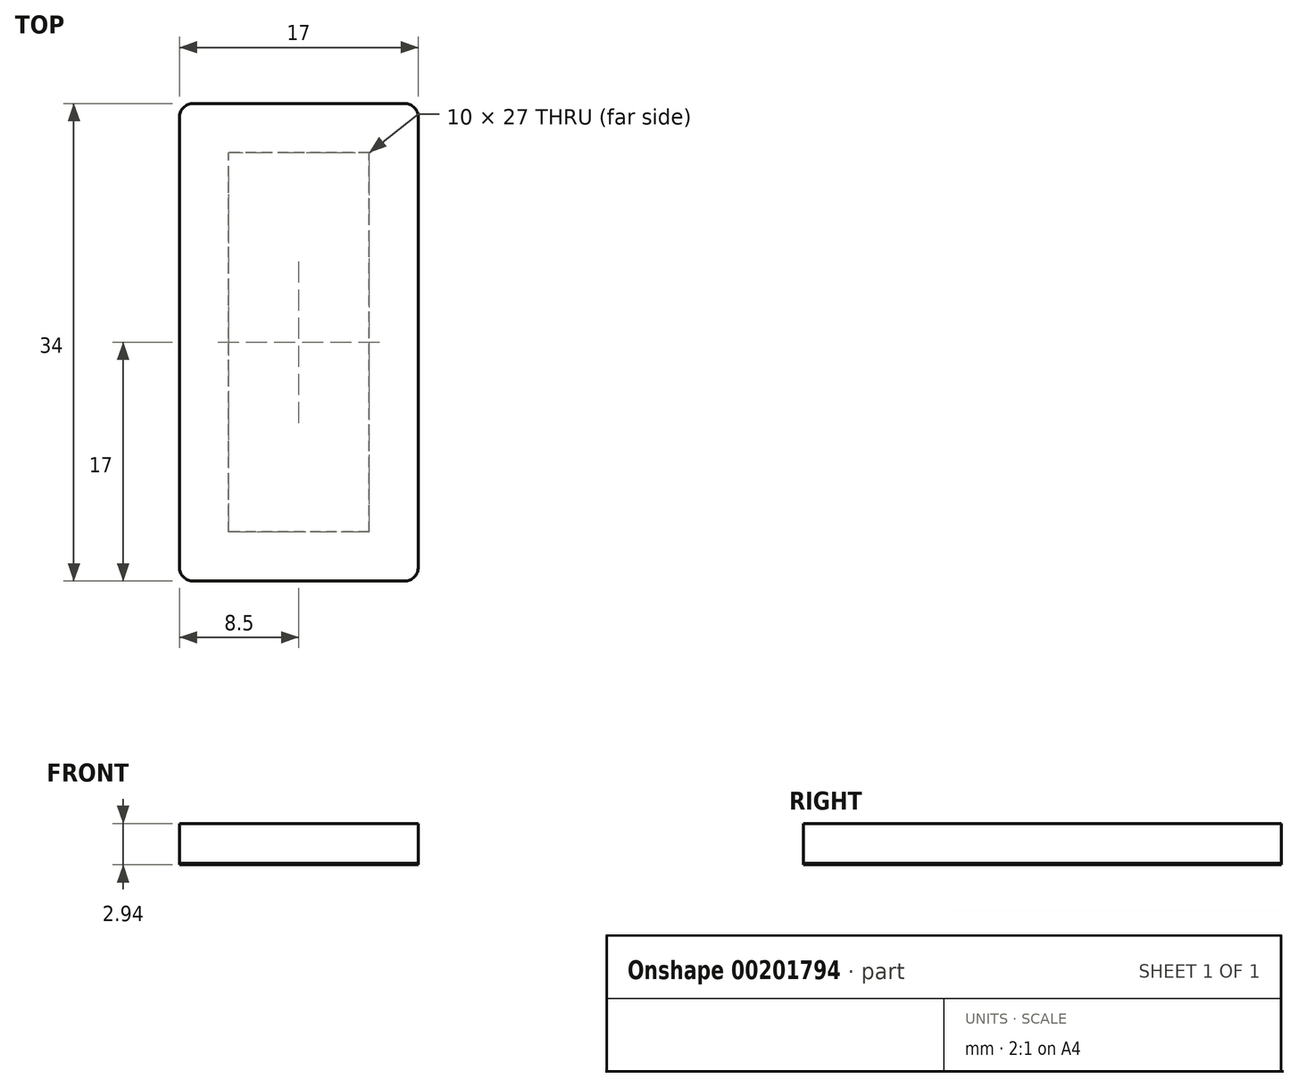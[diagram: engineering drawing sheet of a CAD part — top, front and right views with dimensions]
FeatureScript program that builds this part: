
annotation { "Feature Type Name" : "Feature", "Feature Type Description" : "" }
export const myFeature = defineFeature(function(context is Context, id is Id, definition is map)
    precondition{}
    {
        {
            var Q0;
            Q0=qCreatedBy(makeId("Top.planeOp"),FACE);
            var sketch = newSketch(context, id + "F0", { "sketchPlane" : qUnion([Q0])});
            skLineSegment(sketch, "E0", {"start": v(0, 53.35) * mm, "end": v(0, -57.86) * mm, "construction": true});
            skLineSegment(sketch, "E1", {"start": v(-67.38, 0) * mm, "end": v(68.88, 0) * mm, "construction": true});
            skLineSegment(sketch, "E2.bottom", {"start": v(-8.5, 17) * mm, "end": v(8.5, 17) * mm});
            skLineSegment(sketch, "E2.top", {"start": v(-8.5, -17) * mm, "end": v(8.5, -17) * mm});
            skLineSegment(sketch, "E2.left", {"start": v(-8.5, 17) * mm, "end": v(-8.5, -17) * mm});
            skLineSegment(sketch, "E2.right", {"start": v(8.5, 17) * mm, "end": v(8.5, -17) * mm});
            skPoint(sketch, "E3", {"position": v(0, 17) * mm});
            skPoint(sketch, "E4", {"position": v(-8.5, 0) * mm});
            skSolve(sketch);
        }
        {
            var Q0;
            Q0 = qSketchRegion(id + "F0", true);
            extrude(context, id + "F1", {"entities" : qUnion([Q0]), "oppositeDirection" : true, "depth" : 2.84 * mm});
        }
        {
            var Q0;
            Q0=makeQuery(id+"F1.opExtrude","SWEPT_EDGE",EDGE,{"disambiguationData":[OSD([sQuery(id+"F0.wireOp",EDGE,"E2.top"),sQuery(id+"F0.wireOp",EDGE,"E2.left")])]});
            var Q1;
            Q1=makeQuery(id+"F1.opExtrude","SWEPT_EDGE",EDGE,{"disambiguationData":[OSD([sQuery(id+"F0.wireOp",EDGE,"E2.top"),sQuery(id+"F0.wireOp",EDGE,"E2.right")])]});
            var Q2;
            Q2=makeQuery(id+"F1.opExtrude","SWEPT_EDGE",EDGE,{"disambiguationData":[OSD([sQuery(id+"F0.wireOp",EDGE,"E2.bottom"),sQuery(id+"F0.wireOp",EDGE,"E2.right")])]});
            var Q3;
            Q3=makeQuery(id+"F1.opExtrude","SWEPT_EDGE",EDGE,{"disambiguationData":[OSD([sQuery(id+"F0.wireOp",EDGE,"E2.bottom"),sQuery(id+"F0.wireOp",EDGE,"E2.left")])]});
            fillet(context, id + "F2", {"entities" : qUnion([Q0, Q1, Q2, Q3]), "radius" : 1 * mm, "tangentPropagation" : true, "allowEdgeOverflow" : false});
        }
        {
            var Q0;
            Q0=makeQuery(id+"F1.opExtrude","CAP_FACE",FACE,{"disambiguationData":[OSD([sQuery(id+"F0.wireOp",EDGE,"E2.bottom"),sQuery(id+"F0.wireOp",EDGE,"E2.top"),sQuery(id+"F0.wireOp",EDGE,"E2.left"),sQuery(id+"F0.wireOp",EDGE,"E2.right")])],"isStart":false});
            var sketch = newSketch(context, id + "F3", { "sketchPlane" : qUnion([Q0])});
            skLineSegment(sketch, "E5.0.0", {"start": v(-8.5, 16) * mm, "end": v(-8.5, -16) * mm});
            skArc(sketch, "E5.0.1", {"start": v(-8.5, -16) * mm, "mid": v(-8.2, -16.7) * mm, "end": v(-7.5, -17) * mm});
            skLineSegment(sketch, "E5.0.2", {"start": v(-7.5, -17) * mm, "end": v(7.5, -17) * mm});
            skArc(sketch, "E5.0.3", {"start": v(7.5, -17) * mm, "mid": v(8.2, -16.7) * mm, "end": v(8.5, -16) * mm});
            skLineSegment(sketch, "E5.0.4", {"start": v(8.5, -16) * mm, "end": v(8.5, 16) * mm});
            skArc(sketch, "E5.0.5", {"start": v(8.5, 16) * mm, "mid": v(8.2, 16.7) * mm, "end": v(7.5, 17) * mm});
            skLineSegment(sketch, "E5.0.6", {"start": v(7.5, 17) * mm, "end": v(-7.5, 17) * mm});
            skArc(sketch, "E5.0.7", {"start": v(-7.5, 17) * mm, "mid": v(-8.2, 16.7) * mm, "end": v(-8.5, 16) * mm});
            skPoint(sketch, "E6.endSnap0", {"position": v(-8.5, 0) * mm});
            skLineSegment(sketch, "E7.bottom", {"start": v(5, 13.5) * mm, "end": v(-5, 13.5) * mm});
            skLineSegment(sketch, "E7.top", {"start": v(5, -13.5) * mm, "end": v(-5, -13.5) * mm});
            skLineSegment(sketch, "E7.left", {"start": v(5, 13.5) * mm, "end": v(5, -13.5) * mm});
            skLineSegment(sketch, "E7.right", {"start": v(-5, 13.5) * mm, "end": v(-5, -13.5) * mm});
            skPoint(sketch, "E8", {"position": v(5, 0) * mm});
            skPoint(sketch, "E9", {"position": v(0, -13.5) * mm});
            skSolve(sketch);
        }
        {
            var Q0;
            Q0 = qSketchRegion(id + "F3", true);
            extrude(context, id + "F4", {"entities" : qUnion([Q0]), "depth" : .1 * mm});
        }
    });
